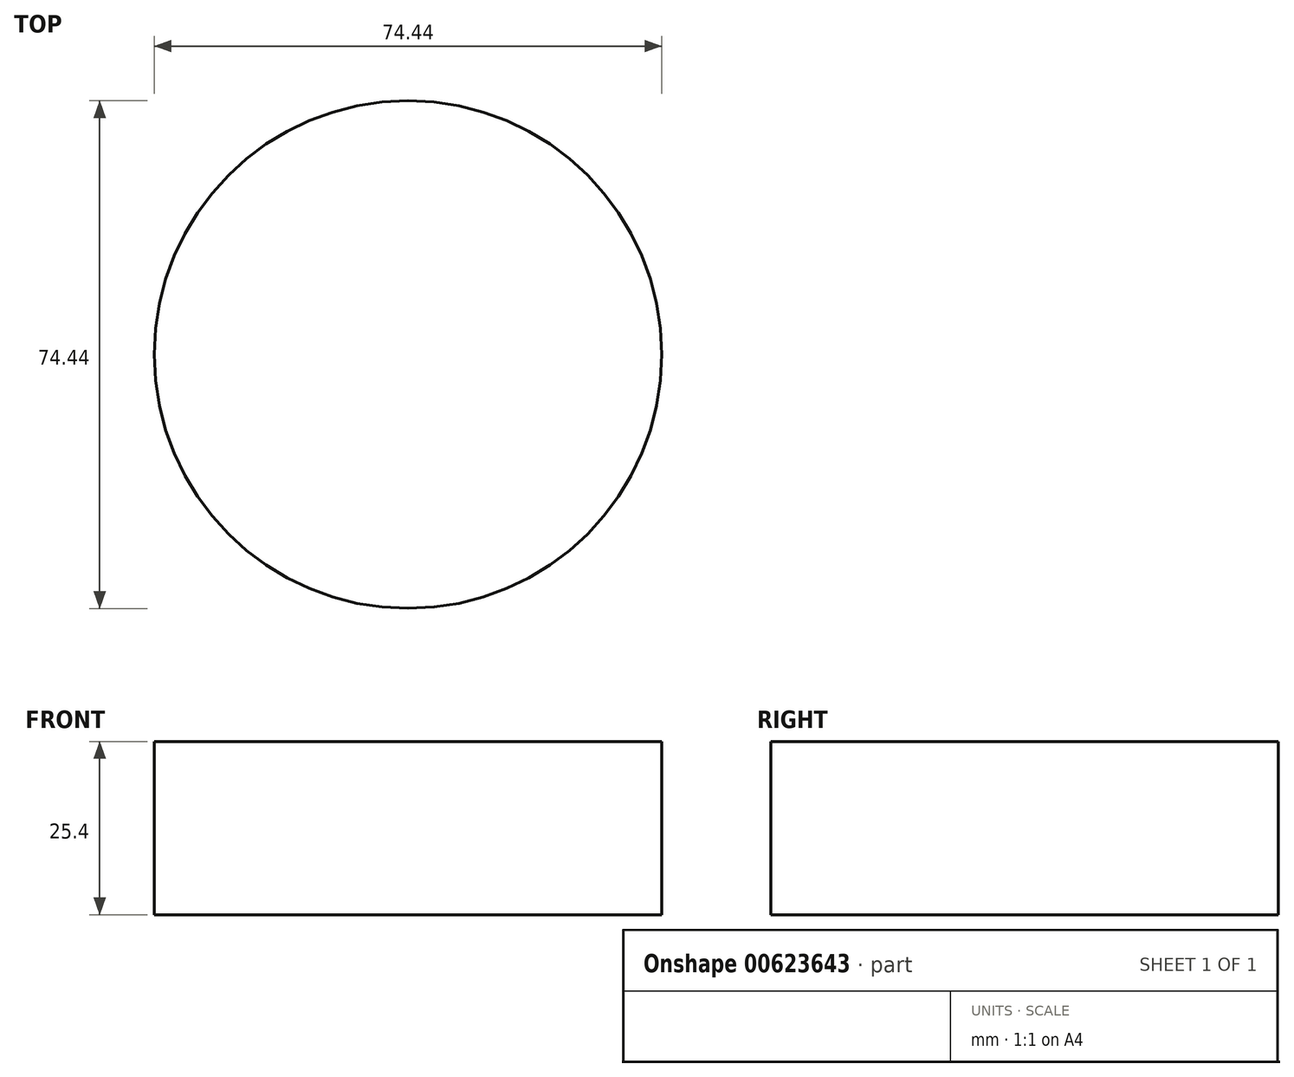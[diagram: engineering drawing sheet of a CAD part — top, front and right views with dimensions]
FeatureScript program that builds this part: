
annotation { "Feature Type Name" : "Feature", "Feature Type Description" : "" }
export const myFeature = defineFeature(function(context is Context, id is Id, definition is map)
    precondition{}
    {
        {
            var Q0;
            Q0=qCreatedBy(makeId("Top.planeOp"),FACE);
            var sketch = newSketch(context, id + "F0", { "sketchPlane" : qUnion([Q0])});
            skCircle(sketch, "E0", {"center": v(0, 0) * mm, "radius": 37.22 * mm});
            skSolve(sketch);
        }
        {
            var Q0;
            Q0=makeQuery(id+"F0.imprint","IMPRINT",FACE,{"disambiguationData":[TD([[makeQuery(id+"F0.imprint","IMPRINT",EDGE,{"derivedFrom":sQuery(id+"F0.wireOp",EDGE,"E0")}),1.0]])]});
            extrude(context, id + "F1", {"entities" : qUnion([Q0]), "depth" : 25.4 * mm, "offsetDistance" : 25.4 * mm});
        }
    });
